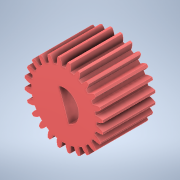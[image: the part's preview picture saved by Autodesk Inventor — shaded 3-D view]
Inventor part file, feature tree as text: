
AUTODESK INVENTOR PART (.ipt)
format: ipt  version: 2022 (Build 260153000, 153)  size: 252,928 bytes
history: mixed  units: in
note: dims shown in document units (in); Inventor stores cm internally (conversion verified against a paired STEP export)
features: direct_edit x1, extrude x1, sketch x1, other x1, move_body x1, imported_body x1
ambient origin geometry x8: Origin, YZ Plane, XZ Plane, XY Plane, X Axis, Y Axis, Z Axis, Center Point
bodies: Solid1 (imported_parasolid)
feature tree (6):
  direct_edit  "Direct Edit1"
  extrude  "Extrusion3"  Depth=0.1703in TaperAngle=0.0deg
  sketch  "Sketch3"  dims[d0=0.0in d1=0.0in d2=-0.25in d9=0.1703in d10=0.0in]
  other  "24_Teeth_Sun_Gear.STEP"
  move_body  "Move1"
  imported_body  NMx_Import_Brep_tag  [imported B-rep: ~101 faces, bbox_mm=[8.65, 12.93135, 12.93135]]
